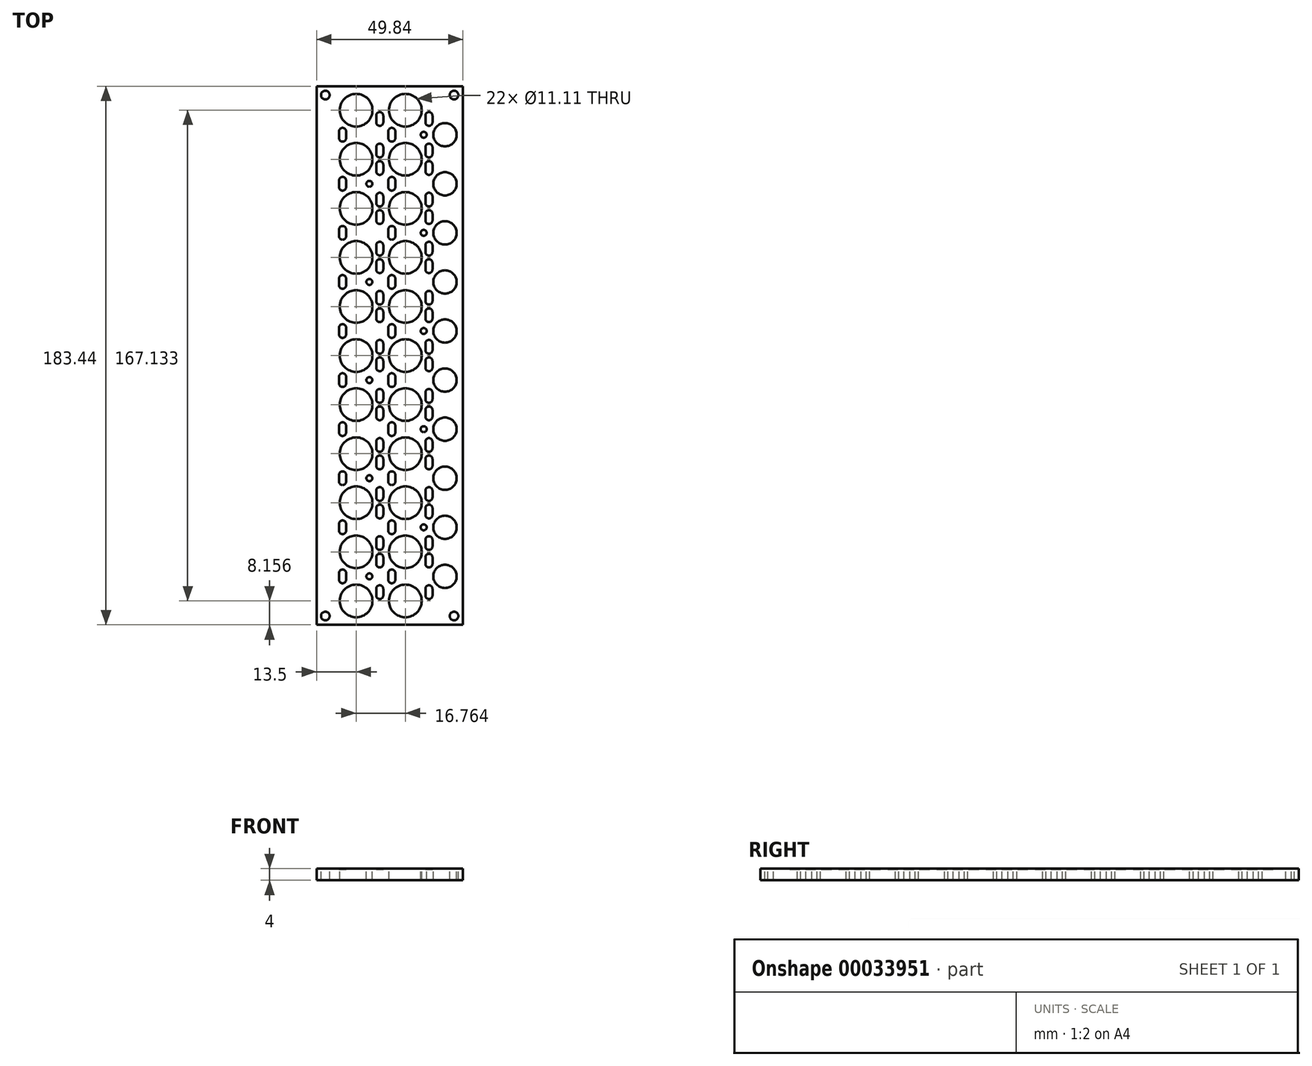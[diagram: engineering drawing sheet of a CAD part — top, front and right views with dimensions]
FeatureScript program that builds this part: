
annotation { "Feature Type Name" : "Feature", "Feature Type Description" : "" }
export const myFeature = defineFeature(function(context is Context, id is Id, definition is map)
    precondition{}
    {
        {
            var Q0;
            Q0=qCreatedBy(makeId("Top.planeOp"),FACE);
            var sketch = newSketch(context, id + "F0", { "sketchPlane" : qUnion([Q0])});
            skLineSegment(sketch, "E0.bottom", {"start": v(-3, -3) * mm, "end": v(46.84, -3) * mm});
            skLineSegment(sketch, "E0.top", {"start": v(-3, 180.44) * mm, "end": v(46.84, 180.44) * mm});
            skLineSegment(sketch, "E0.left", {"start": v(-3, -3) * mm, "end": v(-3, 180.44) * mm});
            skLineSegment(sketch, "E0.right", {"start": v(46.84, -3) * mm, "end": v(46.84, 180.44) * mm});
            skSolve(sketch);
        }
        {
            var Q0;
            Q0 = qSketchRegion(id + "F0", true);
            extrude(context, id + "F1", {"entities" : qUnion([Q0]), "oppositeDirection" : true, "depth" : 4 * mm});
        }
        {
            var Q0;
            Q0=makeQuery(id+"F1.opExtrude","CAP_FACE",FACE,{"disambiguationData":[OSD([sQuery(id+"F0.wireOp",EDGE,"E0.bottom"),sQuery(id+"F0.wireOp",EDGE,"E0.top"),sQuery(id+"F0.wireOp",EDGE,"E0.left"),sQuery(id+"F0.wireOp",EDGE,"E0.right")])],"isStart":true});
            var sketch = newSketch(context, id + "F2", { "sketchPlane" : qUnion([Q0])});
            skPoint(sketch, "E1.rect.middle", {"position": v(35.3, 141.84) * mm});
            skPoint(sketch, "E2.rect.middle", {"position": v(5.88, 30.23) * mm});
            skPoint(sketch, "E3.rect.middle", {"position": v(35.3, 8.14) * mm});
            skPoint(sketch, "E4.rect.middle", {"position": v(5.88, 97.08) * mm});
            skPoint(sketch, "E5.rect.middle", {"position": v(35.3, 102.46) * mm});
            skPoint(sketch, "E6.rect.middle", {"position": v(35.3, 158.56) * mm});
            skPoint(sketch, "E7.rect.middle", {"position": v(5.88, 63.65) * mm});
            skPoint(sketch, "E8.rect.middle", {"position": v(35.3, 35.6) * mm});
            skPoint(sketch, "E9.rect.middle", {"position": v(35.3, 24.85) * mm});
            skPoint(sketch, "E10.rect.middle", {"position": v(35.3, 125.13) * mm});
            skPoint(sketch, "E11.rect.middle", {"position": v(5.88, 130.5) * mm});
            skPoint(sketch, "E12.rect.middle", {"position": v(18.54, 169.3) * mm});
            skPoint(sketch, "E13.rect.middle", {"position": v(35.3, 41.56) * mm});
            skPoint(sketch, "E14.rect.middle", {"position": v(35.3, 74.99) * mm});
            skPoint(sketch, "E15.rect.middle", {"position": v(35.3, 108.42) * mm});
            skPoint(sketch, "E16.rect.middle", {"position": v(35.3, 169.3) * mm});
            skPoint(sketch, "E17.rect.middle", {"position": v(35.3, 91.7) * mm});
            skPoint(sketch, "E18.rect.middle", {"position": v(35.3, 69.03) * mm});
            skPoint(sketch, "E19.rect.middle", {"position": v(35.3, 58.28) * mm});
            skPoint(sketch, "E20.rect.middle", {"position": v(35.3, 135.88) * mm});
            skPoint(sketch, "E21.rect.middle", {"position": v(5.88, 163.93) * mm});
            skPoint(sketch, "E22.rect.middle", {"position": v(35.3, 52.32) * mm});
            skPoint(sketch, "E23.rect.middle", {"position": v(18.54, 141.84) * mm});
            skPoint(sketch, "E24.rect.middle", {"position": v(18.54, 69.03) * mm});
            skPoint(sketch, "E25.rect.middle", {"position": v(18.54, 35.6) * mm});
            skPoint(sketch, "E26.rect.middle", {"position": v(5.88, 113.8) * mm});
            skPoint(sketch, "E27.rect.middle", {"position": v(35.3, 152.6) * mm});
            skPoint(sketch, "E28.rect.middle", {"position": v(35.3, 85.74) * mm});
            skPoint(sketch, "E29.rect.middle", {"position": v(35.3, 119.17) * mm});
            skPoint(sketch, "E30.rect.middle", {"position": v(18.54, 58.28) * mm});
            skPoint(sketch, "E31.rect.middle", {"position": v(5.88, 147.22) * mm});
            skPoint(sketch, "E32.rect.middle", {"position": v(18.54, 135.88) * mm});
            skPoint(sketch, "E33.rect.middle", {"position": v(35.3, 18.89) * mm});
            skPoint(sketch, "E34.rect.middle", {"position": v(22.64, 13.51) * mm});
            skPoint(sketch, "E35.rect.middle", {"position": v(18.54, 102.46) * mm});
            skPoint(sketch, "E36.rect.middle", {"position": v(5.88, 46.94) * mm});
            skPoint(sketch, "E37.rect.middle", {"position": v(18.54, 74.99) * mm});
            skPoint(sketch, "E38.rect.middle", {"position": v(22.64, 80.37) * mm});
            skPoint(sketch, "E39.rect.middle", {"position": v(22.64, 147.22) * mm});
            skPoint(sketch, "E40.rect.middle", {"position": v(18.54, 108.42) * mm});
            skPoint(sketch, "E41.rect.middle", {"position": v(18.54, 8.14) * mm});
            skPoint(sketch, "E42.rect.middle", {"position": v(5.88, 13.51) * mm});
            skPoint(sketch, "E43.rect.middle", {"position": v(5.88, 80.37) * mm});
            skPoint(sketch, "E44.rect.middle", {"position": v(18.54, 41.56) * mm});
            skPoint(sketch, "E45.rect.middle", {"position": v(18.54, 125.13) * mm});
            skPoint(sketch, "E46.rect.middle", {"position": v(18.54, 24.85) * mm});
            skPoint(sketch, "E47.rect.middle", {"position": v(18.54, 85.74) * mm});
            skPoint(sketch, "E48.rect.middle", {"position": v(22.64, 30.23) * mm});
            skPoint(sketch, "E49.rect.middle", {"position": v(22.64, 113.8) * mm});
            skPoint(sketch, "E50.rect.middle", {"position": v(18.54, 91.7) * mm});
            skPoint(sketch, "E51.rect.middle", {"position": v(22.64, 97.08) * mm});
            skPoint(sketch, "E52.rect.middle", {"position": v(22.64, 163.93) * mm});
            skPoint(sketch, "E53.rect.middle", {"position": v(22.64, 130.5) * mm});
            skPoint(sketch, "E54.rect.middle", {"position": v(18.54, 152.6) * mm});
            skPoint(sketch, "E55.rect.middle", {"position": v(18.54, 119.17) * mm});
            skPoint(sketch, "E56.rect.middle", {"position": v(22.64, 63.65) * mm});
            skPoint(sketch, "E57.rect.middle", {"position": v(18.54, 18.89) * mm});
            skPoint(sketch, "E58.rect.middle", {"position": v(22.64, 46.94) * mm});
            skPoint(sketch, "E59.rect.middle", {"position": v(18.54, 158.56) * mm});
            skArc(sketch, "E60", {"start": v(4.68, 62.5) * mm, "mid": v(5.88, 61.31) * mm, "end": v(7.07, 62.5) * mm});
            skArc(sketch, "E61", {"start": v(19.73, 170.46) * mm, "mid": v(18.54, 171.65) * mm, "end": v(17.35, 170.46) * mm});
            skArc(sketch, "E62", {"start": v(34.12, 101.3) * mm, "mid": v(35.3, 100.11) * mm, "end": v(36.5, 101.3) * mm});
            skLineSegment(sketch, "E16.rect.left", {"start": v(36.5, 168.16) * mm, "end": v(36.5, 170.46) * mm});
            skArc(sketch, "E63", {"start": v(7.07, 31.38) * mm, "mid": v(5.88, 32.57) * mm, "end": v(4.68, 31.38) * mm});
            skLineSegment(sketch, "E8.rect.right", {"start": v(34.12, 34.45) * mm, "end": v(34.12, 36.75) * mm});
            skArc(sketch, "E64", {"start": v(34.12, 34.45) * mm, "mid": v(35.3, 33.26) * mm, "end": v(36.5, 34.45) * mm});
            skLineSegment(sketch, "E16.rect.right", {"start": v(34.12, 168.16) * mm, "end": v(34.12, 170.46) * mm});
            skPoint(sketch, "E65.rect.middle", {"position": v(18.54, 52.32) * mm});
            skArc(sketch, "E66", {"start": v(34.12, 168.16) * mm, "mid": v(35.3, 166.97) * mm, "end": v(36.5, 168.16) * mm});
            skLineSegment(sketch, "E8.rect.left", {"start": v(36.5, 34.45) * mm, "end": v(36.5, 36.75) * mm});
            skArc(sketch, "E67", {"start": v(4.68, 129.36) * mm, "mid": v(5.88, 128.16) * mm, "end": v(7.07, 129.36) * mm});
            skArc(sketch, "E68", {"start": v(36.5, 126.28) * mm, "mid": v(35.3, 127.47) * mm, "end": v(34.12, 126.28) * mm});
            skArc(sketch, "E69", {"start": v(36.5, 170.46) * mm, "mid": v(35.3, 171.65) * mm, "end": v(34.12, 170.46) * mm});
            skArc(sketch, "E70", {"start": v(7.07, 81.52) * mm, "mid": v(5.88, 82.7) * mm, "end": v(4.68, 81.52) * mm});
            skArc(sketch, "E71", {"start": v(7.07, 131.66) * mm, "mid": v(5.88, 132.85) * mm, "end": v(4.68, 131.66) * mm});
            skLineSegment(sketch, "E29.rect.right", {"start": v(34.12, 118.02) * mm, "end": v(34.12, 120.32) * mm});
            skLineSegment(sketch, "E12.rect.right", {"start": v(17.35, 168.16) * mm, "end": v(17.35, 170.46) * mm});
            skArc(sketch, "E72", {"start": v(17.35, 168.16) * mm, "mid": v(18.54, 166.97) * mm, "end": v(19.73, 168.16) * mm});
            skArc(sketch, "E73", {"start": v(36.5, 59.43) * mm, "mid": v(35.3, 60.62) * mm, "end": v(34.12, 59.43) * mm});
            skArc(sketch, "E74", {"start": v(19.73, 126.28) * mm, "mid": v(18.54, 127.47) * mm, "end": v(17.35, 126.28) * mm});
            skArc(sketch, "E75", {"start": v(36.5, 76.14) * mm, "mid": v(35.3, 77.33) * mm, "end": v(34.12, 76.14) * mm});
            skArc(sketch, "E76", {"start": v(36.5, 159.7) * mm, "mid": v(35.3, 160.9) * mm, "end": v(34.12, 159.7) * mm});
            skLineSegment(sketch, "E5.rect.left", {"start": v(36.5, 101.3) * mm, "end": v(36.5, 103.6) * mm});
            skArc(sketch, "E77", {"start": v(7.07, 48.09) * mm, "mid": v(5.88, 49.28) * mm, "end": v(4.68, 48.09) * mm});
            skArc(sketch, "E78", {"start": v(7.07, 114.94) * mm, "mid": v(5.88, 116.13) * mm, "end": v(4.68, 114.94) * mm});
            skLineSegment(sketch, "E22.rect.right", {"start": v(34.12, 51.17) * mm, "end": v(34.12, 53.47) * mm});
            skArc(sketch, "E79", {"start": v(34.12, 151.45) * mm, "mid": v(35.3, 150.25) * mm, "end": v(36.5, 151.45) * mm});
            skLineSegment(sketch, "E13.rect.left", {"start": v(36.5, 40.41) * mm, "end": v(36.5, 42.71) * mm});
            skLineSegment(sketch, "E4.rect.left", {"start": v(7.07, 95.93) * mm, "end": v(7.07, 98.23) * mm});
            skArc(sketch, "E80", {"start": v(36.5, 9.29) * mm, "mid": v(35.3, 10.48) * mm, "end": v(34.12, 9.29) * mm});
            skLineSegment(sketch, "E4.rect.right", {"start": v(4.68, 95.93) * mm, "end": v(4.68, 98.23) * mm});
            skArc(sketch, "E81", {"start": v(36.5, 53.47) * mm, "mid": v(35.3, 54.66) * mm, "end": v(34.12, 53.47) * mm});
            skArc(sketch, "E82", {"start": v(34.12, 6.99) * mm, "mid": v(35.3, 5.8) * mm, "end": v(36.5, 6.99) * mm});
            skLineSegment(sketch, "E13.rect.right", {"start": v(34.12, 40.41) * mm, "end": v(34.12, 42.71) * mm});
            skLineSegment(sketch, "E3.rect.left", {"start": v(36.5, 6.99) * mm, "end": v(36.5, 9.29) * mm});
            skArc(sketch, "E83", {"start": v(34.12, 40.41) * mm, "mid": v(35.3, 39.22) * mm, "end": v(36.5, 40.41) * mm});
            skArc(sketch, "E84", {"start": v(34.12, 107.27) * mm, "mid": v(35.3, 106.07) * mm, "end": v(36.5, 107.27) * mm});
            skArc(sketch, "E85", {"start": v(34.12, 51.17) * mm, "mid": v(35.3, 49.98) * mm, "end": v(36.5, 51.17) * mm});
            skLineSegment(sketch, "E15.rect.left", {"start": v(36.5, 107.27) * mm, "end": v(36.5, 109.57) * mm});
            skLineSegment(sketch, "E3.rect.right", {"start": v(34.12, 6.99) * mm, "end": v(34.12, 9.29) * mm});
            skArc(sketch, "E86", {"start": v(34.12, 17.74) * mm, "mid": v(35.3, 16.55) * mm, "end": v(36.5, 17.74) * mm});
            skArc(sketch, "E87", {"start": v(4.68, 29.08) * mm, "mid": v(5.88, 27.88) * mm, "end": v(7.07, 29.08) * mm});
            skArc(sketch, "E88", {"start": v(4.68, 162.78) * mm, "mid": v(5.88, 161.6) * mm, "end": v(7.07, 162.78) * mm});
            skLineSegment(sketch, "E11.rect.left", {"start": v(7.07, 129.36) * mm, "end": v(7.07, 131.66) * mm});
            skLineSegment(sketch, "E21.rect.right", {"start": v(4.68, 162.78) * mm, "end": v(4.68, 165.08) * mm});
            skLineSegment(sketch, "E7.rect.right", {"start": v(4.68, 62.5) * mm, "end": v(4.68, 64.8) * mm});
            skArc(sketch, "E89", {"start": v(34.12, 67.88) * mm, "mid": v(35.3, 66.69) * mm, "end": v(36.5, 67.88) * mm});
            skLineSegment(sketch, "E5.rect.right", {"start": v(34.12, 101.3) * mm, "end": v(34.12, 103.6) * mm});
            skLineSegment(sketch, "E7.rect.left", {"start": v(7.07, 62.5) * mm, "end": v(7.07, 64.8) * mm});
            skLineSegment(sketch, "E18.rect.right", {"start": v(34.12, 67.88) * mm, "end": v(34.12, 70.18) * mm});
            skArc(sketch, "E90", {"start": v(36.5, 103.6) * mm, "mid": v(35.3, 104.8) * mm, "end": v(34.12, 103.6) * mm});
            skLineSegment(sketch, "E12.rect.left", {"start": v(19.73, 168.16) * mm, "end": v(19.73, 170.46) * mm});
            skLineSegment(sketch, "E18.rect.left", {"start": v(36.5, 67.88) * mm, "end": v(36.5, 70.18) * mm});
            skLineSegment(sketch, "E15.rect.right", {"start": v(34.12, 107.27) * mm, "end": v(34.12, 109.57) * mm});
            skArc(sketch, "E91", {"start": v(36.5, 36.75) * mm, "mid": v(35.3, 37.94) * mm, "end": v(34.12, 36.75) * mm});
            skArc(sketch, "E92", {"start": v(4.68, 95.93) * mm, "mid": v(5.88, 94.74) * mm, "end": v(7.07, 95.93) * mm});
            skLineSegment(sketch, "E26.rect.right", {"start": v(4.68, 112.64) * mm, "end": v(4.68, 114.94) * mm});
            skArc(sketch, "E93", {"start": v(36.5, 109.57) * mm, "mid": v(35.3, 110.76) * mm, "end": v(34.12, 109.57) * mm});
            skLineSegment(sketch, "E26.rect.left", {"start": v(7.07, 112.64) * mm, "end": v(7.07, 114.94) * mm});
            skArc(sketch, "E94", {"start": v(7.07, 98.23) * mm, "mid": v(5.88, 99.42) * mm, "end": v(4.68, 98.23) * mm});
            skLineSegment(sketch, "E36.rect.right", {"start": v(4.68, 45.79) * mm, "end": v(4.68, 48.09) * mm});
            skArc(sketch, "E95", {"start": v(36.5, 143) * mm, "mid": v(35.3, 144.18) * mm, "end": v(34.12, 143) * mm});
            skArc(sketch, "E96", {"start": v(4.68, 45.79) * mm, "mid": v(5.88, 44.6) * mm, "end": v(7.07, 45.79) * mm});
            skArc(sketch, "E97", {"start": v(19.73, 9.29) * mm, "mid": v(18.54, 10.48) * mm, "end": v(17.35, 9.29) * mm});
            skArc(sketch, "E98", {"start": v(4.68, 112.64) * mm, "mid": v(5.88, 111.45) * mm, "end": v(7.07, 112.64) * mm});
            skLineSegment(sketch, "E22.rect.left", {"start": v(36.5, 51.17) * mm, "end": v(36.5, 53.47) * mm});
            skLineSegment(sketch, "E11.rect.right", {"start": v(4.68, 129.36) * mm, "end": v(4.68, 131.66) * mm});
            skArc(sketch, "E99", {"start": v(7.07, 165.08) * mm, "mid": v(5.88, 166.27) * mm, "end": v(4.68, 165.08) * mm});
            skArc(sketch, "E100", {"start": v(7.07, 64.8) * mm, "mid": v(5.88, 66) * mm, "end": v(4.68, 64.8) * mm});
            skArc(sketch, "E101", {"start": v(17.35, 6.99) * mm, "mid": v(18.54, 5.8) * mm, "end": v(19.73, 6.99) * mm});
            skArc(sketch, "E102", {"start": v(36.5, 42.71) * mm, "mid": v(35.3, 43.9) * mm, "end": v(34.12, 42.71) * mm});
            skArc(sketch, "E103", {"start": v(36.5, 92.85) * mm, "mid": v(35.3, 94.04) * mm, "end": v(34.12, 92.85) * mm});
            skLineSegment(sketch, "E36.rect.left", {"start": v(7.07, 45.79) * mm, "end": v(7.07, 48.09) * mm});
            skLineSegment(sketch, "E29.rect.left", {"start": v(36.5, 118.02) * mm, "end": v(36.5, 120.32) * mm});
            skArc(sketch, "E104", {"start": v(34.12, 118.02) * mm, "mid": v(35.3, 116.83) * mm, "end": v(36.5, 118.02) * mm});
            skLineSegment(sketch, "E21.rect.left", {"start": v(7.07, 162.78) * mm, "end": v(7.07, 165.08) * mm});
            skArc(sketch, "E105", {"start": v(4.68, 146.07) * mm, "mid": v(5.88, 144.88) * mm, "end": v(7.07, 146.07) * mm});
            skLineSegment(sketch, "E2.rect.left", {"start": v(7.07, 29.08) * mm, "end": v(7.07, 31.38) * mm});
            skLineSegment(sketch, "E2.rect.right", {"start": v(4.68, 29.08) * mm, "end": v(4.68, 31.38) * mm});
            skLineSegment(sketch, "E41.rect.left", {"start": v(19.73, 6.99) * mm, "end": v(19.73, 9.29) * mm});
            skLineSegment(sketch, "E41.rect.right", {"start": v(17.35, 6.99) * mm, "end": v(17.35, 9.29) * mm});
            skArc(sketch, "E106", {"start": v(23.83, 48.09) * mm, "mid": v(22.64, 49.28) * mm, "end": v(21.45, 48.09) * mm});
            skArc(sketch, "E107", {"start": v(21.45, 29.08) * mm, "mid": v(22.64, 27.88) * mm, "end": v(23.83, 29.08) * mm});
            skLineSegment(sketch, "E48.rect.right", {"start": v(21.45, 29.08) * mm, "end": v(21.45, 31.38) * mm});
            skArc(sketch, "E108", {"start": v(19.73, 109.57) * mm, "mid": v(18.54, 110.76) * mm, "end": v(17.35, 109.57) * mm});
            skLineSegment(sketch, "E47.rect.left", {"start": v(19.73, 84.6) * mm, "end": v(19.73, 86.9) * mm});
            skLineSegment(sketch, "E24.rect.left", {"start": v(19.73, 67.88) * mm, "end": v(19.73, 70.18) * mm});
            skArc(sketch, "E109", {"start": v(23.83, 14.66) * mm, "mid": v(22.64, 15.85) * mm, "end": v(21.45, 14.66) * mm});
            skLineSegment(sketch, "E20.rect.right", {"start": v(34.12, 134.73) * mm, "end": v(34.12, 137.03) * mm});
            skLineSegment(sketch, "E31.rect.right", {"start": v(4.68, 146.07) * mm, "end": v(4.68, 148.37) * mm});
            skLineSegment(sketch, "E6.rect.left", {"start": v(36.5, 157.4) * mm, "end": v(36.5, 159.7) * mm});
            skArc(sketch, "E110", {"start": v(21.45, 12.36) * mm, "mid": v(22.64, 11.17) * mm, "end": v(23.83, 12.36) * mm});
            skArc(sketch, "E111", {"start": v(4.68, 79.22) * mm, "mid": v(5.88, 78.02) * mm, "end": v(7.07, 79.22) * mm});
            skLineSegment(sketch, "E28.rect.right", {"start": v(34.12, 84.6) * mm, "end": v(34.12, 86.9) * mm});
            skLineSegment(sketch, "E39.rect.left", {"start": v(23.83, 146.07) * mm, "end": v(23.83, 148.37) * mm});
            skArc(sketch, "E112", {"start": v(21.45, 79.22) * mm, "mid": v(22.64, 78.02) * mm, "end": v(23.83, 79.22) * mm});
            skArc(sketch, "E113", {"start": v(17.35, 73.84) * mm, "mid": v(18.54, 72.65) * mm, "end": v(19.73, 73.84) * mm});
            skArc(sketch, "E114", {"start": v(21.45, 146.07) * mm, "mid": v(22.64, 144.88) * mm, "end": v(23.83, 146.07) * mm});
            skLineSegment(sketch, "E10.rect.right", {"start": v(34.12, 123.98) * mm, "end": v(34.12, 126.28) * mm});
            skLineSegment(sketch, "E37.rect.right", {"start": v(17.35, 73.84) * mm, "end": v(17.35, 76.14) * mm});
            skLineSegment(sketch, "E31.rect.left", {"start": v(7.07, 146.07) * mm, "end": v(7.07, 148.37) * mm});
            skArc(sketch, "E115", {"start": v(17.35, 40.41) * mm, "mid": v(18.54, 39.22) * mm, "end": v(19.73, 40.41) * mm});
            skArc(sketch, "E116", {"start": v(4.68, 12.36) * mm, "mid": v(5.88, 11.17) * mm, "end": v(7.07, 12.36) * mm});
            skLineSegment(sketch, "E17.rect.left", {"start": v(36.5, 90.55) * mm, "end": v(36.5, 92.85) * mm});
            skLineSegment(sketch, "E10.rect.left", {"start": v(36.5, 123.98) * mm, "end": v(36.5, 126.28) * mm});
            skArc(sketch, "E117", {"start": v(34.12, 140.7) * mm, "mid": v(35.3, 139.5) * mm, "end": v(36.5, 140.7) * mm});
            skArc(sketch, "E118", {"start": v(7.07, 14.66) * mm, "mid": v(5.88, 15.85) * mm, "end": v(4.68, 14.66) * mm});
            skArc(sketch, "E119", {"start": v(19.73, 70.18) * mm, "mid": v(18.54, 71.37) * mm, "end": v(17.35, 70.18) * mm});
            skArc(sketch, "E120", {"start": v(36.5, 20.04) * mm, "mid": v(35.3, 21.23) * mm, "end": v(34.12, 20.04) * mm});
            skLineSegment(sketch, "E35.rect.right", {"start": v(17.35, 101.3) * mm, "end": v(17.35, 103.6) * mm});
            skArc(sketch, "E121", {"start": v(34.12, 84.6) * mm, "mid": v(35.3, 83.4) * mm, "end": v(36.5, 84.6) * mm});
            skLineSegment(sketch, "E40.rect.left", {"start": v(19.73, 107.27) * mm, "end": v(19.73, 109.57) * mm});
            skLineSegment(sketch, "E24.rect.right", {"start": v(17.35, 67.88) * mm, "end": v(17.35, 70.18) * mm});
            skLineSegment(sketch, "E20.rect.left", {"start": v(36.5, 134.73) * mm, "end": v(36.5, 137.03) * mm});
            skLineSegment(sketch, "E38.rect.right", {"start": v(21.45, 79.22) * mm, "end": v(21.45, 81.52) * mm});
            skLineSegment(sketch, "E32.rect.right", {"start": v(17.35, 134.73) * mm, "end": v(17.35, 137.03) * mm});
            skLineSegment(sketch, "E27.rect.right", {"start": v(34.12, 151.45) * mm, "end": v(34.12, 153.75) * mm});
            skLineSegment(sketch, "E33.rect.left", {"start": v(36.5, 17.74) * mm, "end": v(36.5, 20.04) * mm});
            skArc(sketch, "E122", {"start": v(34.12, 23.7) * mm, "mid": v(35.3, 22.5) * mm, "end": v(36.5, 23.7) * mm});
            skArc(sketch, "E123", {"start": v(19.73, 36.75) * mm, "mid": v(18.54, 37.94) * mm, "end": v(17.35, 36.75) * mm});
            skLineSegment(sketch, "E14.rect.right", {"start": v(34.12, 73.84) * mm, "end": v(34.12, 76.14) * mm});
            skArc(sketch, "E124", {"start": v(17.35, 107.27) * mm, "mid": v(18.54, 106.07) * mm, "end": v(19.73, 107.27) * mm});
            skArc(sketch, "E125", {"start": v(34.12, 157.4) * mm, "mid": v(35.3, 156.21) * mm, "end": v(36.5, 157.4) * mm});
            skLineSegment(sketch, "E40.rect.right", {"start": v(17.35, 107.27) * mm, "end": v(17.35, 109.57) * mm});
            skLineSegment(sketch, "E23.rect.left", {"start": v(19.73, 140.7) * mm, "end": v(19.73, 143) * mm});
            skLineSegment(sketch, "E33.rect.right", {"start": v(34.12, 17.74) * mm, "end": v(34.12, 20.04) * mm});
            skLineSegment(sketch, "E44.rect.left", {"start": v(19.73, 40.41) * mm, "end": v(19.73, 42.71) * mm});
            skArc(sketch, "E126", {"start": v(36.5, 26) * mm, "mid": v(35.3, 27.19) * mm, "end": v(34.12, 26) * mm});
            skArc(sketch, "E127", {"start": v(17.35, 34.45) * mm, "mid": v(18.54, 33.26) * mm, "end": v(19.73, 34.45) * mm});
            skArc(sketch, "E128", {"start": v(36.5, 86.9) * mm, "mid": v(35.3, 88.08) * mm, "end": v(34.12, 86.9) * mm});
            skArc(sketch, "E129", {"start": v(17.35, 84.6) * mm, "mid": v(18.54, 83.4) * mm, "end": v(19.73, 84.6) * mm});
            skArc(sketch, "E130", {"start": v(19.73, 143) * mm, "mid": v(18.54, 144.18) * mm, "end": v(17.35, 143) * mm});
            skLineSegment(sketch, "E28.rect.left", {"start": v(36.5, 84.6) * mm, "end": v(36.5, 86.9) * mm});
            skLineSegment(sketch, "E1.rect.left", {"start": v(36.5, 140.7) * mm, "end": v(36.5, 143) * mm});
            skArc(sketch, "E131", {"start": v(36.5, 137.03) * mm, "mid": v(35.3, 138.22) * mm, "end": v(34.12, 137.03) * mm});
            skArc(sketch, "E132", {"start": v(34.12, 73.84) * mm, "mid": v(35.3, 72.65) * mm, "end": v(36.5, 73.84) * mm});
            skArc(sketch, "E133", {"start": v(7.07, 148.37) * mm, "mid": v(5.88, 149.56) * mm, "end": v(4.68, 148.37) * mm});
            skLineSegment(sketch, "E43.rect.right", {"start": v(4.68, 79.22) * mm, "end": v(4.68, 81.52) * mm});
            skLineSegment(sketch, "E47.rect.right", {"start": v(17.35, 84.6) * mm, "end": v(17.35, 86.9) * mm});
            skLineSegment(sketch, "E39.rect.right", {"start": v(21.45, 146.07) * mm, "end": v(21.45, 148.37) * mm});
            skLineSegment(sketch, "E34.rect.right", {"start": v(21.45, 12.36) * mm, "end": v(21.45, 14.66) * mm});
            skArc(sketch, "E134", {"start": v(36.5, 70.18) * mm, "mid": v(35.3, 71.37) * mm, "end": v(34.12, 70.18) * mm});
            skLineSegment(sketch, "E17.rect.right", {"start": v(34.12, 90.55) * mm, "end": v(34.12, 92.85) * mm});
            skArc(sketch, "E135", {"start": v(34.12, 123.98) * mm, "mid": v(35.3, 122.79) * mm, "end": v(36.5, 123.98) * mm});
            skLineSegment(sketch, "E14.rect.left", {"start": v(36.5, 73.84) * mm, "end": v(36.5, 76.14) * mm});
            skLineSegment(sketch, "E23.rect.right", {"start": v(17.35, 140.7) * mm, "end": v(17.35, 143) * mm});
            skLineSegment(sketch, "E43.rect.left", {"start": v(7.07, 79.22) * mm, "end": v(7.07, 81.52) * mm});
            skLineSegment(sketch, "E34.rect.left", {"start": v(23.83, 12.36) * mm, "end": v(23.83, 14.66) * mm});
            skLineSegment(sketch, "E44.rect.right", {"start": v(17.35, 40.41) * mm, "end": v(17.35, 42.71) * mm});
            skArc(sketch, "E136", {"start": v(36.5, 120.32) * mm, "mid": v(35.3, 121.5) * mm, "end": v(34.12, 120.32) * mm});
            skLineSegment(sketch, "E1.rect.right", {"start": v(34.12, 140.7) * mm, "end": v(34.12, 143) * mm});
            skArc(sketch, "E137", {"start": v(36.5, 153.75) * mm, "mid": v(35.3, 154.94) * mm, "end": v(34.12, 153.75) * mm});
            skArc(sketch, "E138", {"start": v(23.83, 64.8) * mm, "mid": v(22.64, 66) * mm, "end": v(21.45, 64.8) * mm});
            skArc(sketch, "E139", {"start": v(17.35, 17.74) * mm, "mid": v(18.54, 16.55) * mm, "end": v(19.73, 17.74) * mm});
            skArc(sketch, "E140", {"start": v(19.73, 42.71) * mm, "mid": v(18.54, 43.9) * mm, "end": v(17.35, 42.71) * mm});
            skArc(sketch, "E141", {"start": v(34.12, 134.73) * mm, "mid": v(35.3, 133.54) * mm, "end": v(36.5, 134.73) * mm});
            skArc(sketch, "E142", {"start": v(17.35, 101.3) * mm, "mid": v(18.54, 100.11) * mm, "end": v(19.73, 101.3) * mm});
            skLineSegment(sketch, "E35.rect.left", {"start": v(19.73, 101.3) * mm, "end": v(19.73, 103.6) * mm});
            skArc(sketch, "E143", {"start": v(17.35, 140.7) * mm, "mid": v(18.54, 139.5) * mm, "end": v(19.73, 140.7) * mm});
            skLineSegment(sketch, "E9.rect.left", {"start": v(36.5, 23.7) * mm, "end": v(36.5, 26) * mm});
            skArc(sketch, "E144", {"start": v(19.73, 76.14) * mm, "mid": v(18.54, 77.33) * mm, "end": v(17.35, 76.14) * mm});
            skArc(sketch, "E145", {"start": v(17.35, 67.88) * mm, "mid": v(18.54, 66.69) * mm, "end": v(19.73, 67.88) * mm});
            skArc(sketch, "E146", {"start": v(19.73, 137.03) * mm, "mid": v(18.54, 138.22) * mm, "end": v(17.35, 137.03) * mm});
            skLineSegment(sketch, "E38.rect.left", {"start": v(23.83, 79.22) * mm, "end": v(23.83, 81.52) * mm});
            skLineSegment(sketch, "E27.rect.left", {"start": v(36.5, 151.45) * mm, "end": v(36.5, 153.75) * mm});
            skArc(sketch, "E147", {"start": v(17.35, 151.45) * mm, "mid": v(18.54, 150.25) * mm, "end": v(19.73, 151.45) * mm});
            skLineSegment(sketch, "E48.rect.left", {"start": v(23.83, 29.08) * mm, "end": v(23.83, 31.38) * mm});
            skArc(sketch, "E148", {"start": v(23.83, 81.52) * mm, "mid": v(22.64, 82.7) * mm, "end": v(21.45, 81.52) * mm});
            skLineSegment(sketch, "E37.rect.left", {"start": v(19.73, 73.84) * mm, "end": v(19.73, 76.14) * mm});
            skLineSegment(sketch, "E32.rect.left", {"start": v(19.73, 134.73) * mm, "end": v(19.73, 137.03) * mm});
            skArc(sketch, "E149", {"start": v(34.12, 90.55) * mm, "mid": v(35.3, 89.36) * mm, "end": v(36.5, 90.55) * mm});
            skLineSegment(sketch, "E6.rect.right", {"start": v(34.12, 157.4) * mm, "end": v(34.12, 159.7) * mm});
            skArc(sketch, "E150", {"start": v(23.83, 31.38) * mm, "mid": v(22.64, 32.57) * mm, "end": v(21.45, 31.38) * mm});
            skLineSegment(sketch, "E9.rect.right", {"start": v(34.12, 23.7) * mm, "end": v(34.12, 26) * mm});
            skArc(sketch, "E151", {"start": v(17.35, 134.73) * mm, "mid": v(18.54, 133.54) * mm, "end": v(19.73, 134.73) * mm});
            skArc(sketch, "E152", {"start": v(19.73, 103.6) * mm, "mid": v(18.54, 104.8) * mm, "end": v(17.35, 103.6) * mm});
            skArc(sketch, "E153", {"start": v(23.83, 148.37) * mm, "mid": v(22.64, 149.56) * mm, "end": v(21.45, 148.37) * mm});
            skLineSegment(sketch, "E25.rect.right", {"start": v(17.35, 34.45) * mm, "end": v(17.35, 36.75) * mm});
            skLineSegment(sketch, "E42.rect.right", {"start": v(4.68, 12.36) * mm, "end": v(4.68, 14.66) * mm});
            skLineSegment(sketch, "E42.rect.left", {"start": v(7.07, 12.36) * mm, "end": v(7.07, 14.66) * mm});
            skLineSegment(sketch, "E25.rect.left", {"start": v(19.73, 34.45) * mm, "end": v(19.73, 36.75) * mm});
            skLineSegment(sketch, "E53.rect.left", {"start": v(23.83, 129.36) * mm, "end": v(23.83, 131.66) * mm});
            skLineSegment(sketch, "E19.rect.right", {"start": v(34.12, 57.13) * mm, "end": v(34.12, 59.43) * mm});
            skLineSegment(sketch, "E49.rect.right", {"start": v(21.45, 112.64) * mm, "end": v(21.45, 114.94) * mm});
            skLineSegment(sketch, "E50.rect.left", {"start": v(19.73, 90.55) * mm, "end": v(19.73, 92.85) * mm});
            skArc(sketch, "E154", {"start": v(19.73, 53.47) * mm, "mid": v(18.54, 54.66) * mm, "end": v(17.35, 53.47) * mm});
            skArc(sketch, "E155", {"start": v(17.35, 90.55) * mm, "mid": v(18.54, 89.36) * mm, "end": v(19.73, 90.55) * mm});
            skLineSegment(sketch, "E50.rect.right", {"start": v(17.35, 90.55) * mm, "end": v(17.35, 92.85) * mm});
            skLineSegment(sketch, "E52.rect.left", {"start": v(23.83, 162.78) * mm, "end": v(23.83, 165.08) * mm});
            skLineSegment(sketch, "E55.rect.left", {"start": v(19.73, 118.02) * mm, "end": v(19.73, 120.32) * mm});
            skLineSegment(sketch, "E46.rect.right", {"start": v(17.35, 23.7) * mm, "end": v(17.35, 26) * mm});
            skArc(sketch, "E156", {"start": v(17.35, 157.4) * mm, "mid": v(18.54, 156.21) * mm, "end": v(19.73, 157.4) * mm});
            skLineSegment(sketch, "E59.rect.right", {"start": v(17.35, 157.4) * mm, "end": v(17.35, 159.7) * mm});
            skLineSegment(sketch, "E46.rect.left", {"start": v(19.73, 23.7) * mm, "end": v(19.73, 26) * mm});
            skLineSegment(sketch, "E30.rect.left", {"start": v(19.73, 57.13) * mm, "end": v(19.73, 59.43) * mm});
            skArc(sketch, "E157", {"start": v(19.73, 120.32) * mm, "mid": v(18.54, 121.5) * mm, "end": v(17.35, 120.32) * mm});
            skArc(sketch, "E158", {"start": v(21.45, 112.64) * mm, "mid": v(22.64, 111.45) * mm, "end": v(23.83, 112.64) * mm});
            skArc(sketch, "E159", {"start": v(21.45, 95.93) * mm, "mid": v(22.64, 94.74) * mm, "end": v(23.83, 95.93) * mm});
            skLineSegment(sketch, "E52.rect.right", {"start": v(21.45, 162.78) * mm, "end": v(21.45, 165.08) * mm});
            skLineSegment(sketch, "E54.rect.left", {"start": v(19.73, 151.45) * mm, "end": v(19.73, 153.75) * mm});
            skArc(sketch, "E160", {"start": v(19.73, 153.75) * mm, "mid": v(18.54, 154.94) * mm, "end": v(17.35, 153.75) * mm});
            skLineSegment(sketch, "E45.rect.right", {"start": v(17.35, 123.98) * mm, "end": v(17.35, 126.28) * mm});
            skLineSegment(sketch, "E30.rect.right", {"start": v(17.35, 57.13) * mm, "end": v(17.35, 59.43) * mm});
            skArc(sketch, "E161", {"start": v(17.35, 123.98) * mm, "mid": v(18.54, 122.79) * mm, "end": v(19.73, 123.98) * mm});
            skArc(sketch, "E162", {"start": v(19.73, 92.85) * mm, "mid": v(18.54, 94.04) * mm, "end": v(17.35, 92.85) * mm});
            skArc(sketch, "E163", {"start": v(34.12, 57.13) * mm, "mid": v(35.3, 55.93) * mm, "end": v(36.5, 57.13) * mm});
            skLineSegment(sketch, "E55.rect.right", {"start": v(17.35, 118.02) * mm, "end": v(17.35, 120.32) * mm});
            skLineSegment(sketch, "E51.rect.left", {"start": v(23.83, 95.93) * mm, "end": v(23.83, 98.23) * mm});
            skLineSegment(sketch, "E54.rect.right", {"start": v(17.35, 151.45) * mm, "end": v(17.35, 153.75) * mm});
            skLineSegment(sketch, "E49.rect.left", {"start": v(23.83, 112.64) * mm, "end": v(23.83, 114.94) * mm});
            skLineSegment(sketch, "E45.rect.left", {"start": v(19.73, 123.98) * mm, "end": v(19.73, 126.28) * mm});
            skLineSegment(sketch, "E58.rect.right", {"start": v(21.45, 45.79) * mm, "end": v(21.45, 48.09) * mm});
            skArc(sketch, "E164", {"start": v(19.73, 26) * mm, "mid": v(18.54, 27.19) * mm, "end": v(17.35, 26) * mm});
            skArc(sketch, "E165", {"start": v(21.45, 45.79) * mm, "mid": v(22.64, 44.6) * mm, "end": v(23.83, 45.79) * mm});
            skLineSegment(sketch, "E53.rect.right", {"start": v(21.45, 129.36) * mm, "end": v(21.45, 131.66) * mm});
            skArc(sketch, "E166", {"start": v(17.35, 23.7) * mm, "mid": v(18.54, 22.5) * mm, "end": v(19.73, 23.7) * mm});
            skLineSegment(sketch, "E58.rect.left", {"start": v(23.83, 45.79) * mm, "end": v(23.83, 48.09) * mm});
            skLineSegment(sketch, "E59.rect.left", {"start": v(19.73, 157.4) * mm, "end": v(19.73, 159.7) * mm});
            skArc(sketch, "E167", {"start": v(21.45, 162.78) * mm, "mid": v(22.64, 161.6) * mm, "end": v(23.83, 162.78) * mm});
            skArc(sketch, "E168", {"start": v(19.73, 59.43) * mm, "mid": v(18.54, 60.62) * mm, "end": v(17.35, 59.43) * mm});
            skArc(sketch, "E169", {"start": v(19.73, 20.04) * mm, "mid": v(18.54, 21.23) * mm, "end": v(17.35, 20.04) * mm});
            skArc(sketch, "E170", {"start": v(23.83, 131.66) * mm, "mid": v(22.64, 132.85) * mm, "end": v(21.45, 131.66) * mm});
            skLineSegment(sketch, "E19.rect.left", {"start": v(36.5, 57.13) * mm, "end": v(36.5, 59.43) * mm});
            skArc(sketch, "E171", {"start": v(21.45, 129.36) * mm, "mid": v(22.64, 128.16) * mm, "end": v(23.83, 129.36) * mm});
            skArc(sketch, "E172", {"start": v(19.73, 86.9) * mm, "mid": v(18.54, 88.08) * mm, "end": v(17.35, 86.9) * mm});
            skArc(sketch, "E173", {"start": v(23.83, 98.23) * mm, "mid": v(22.64, 99.42) * mm, "end": v(21.45, 98.23) * mm});
            skArc(sketch, "E174", {"start": v(23.83, 165.08) * mm, "mid": v(22.64, 166.27) * mm, "end": v(21.45, 165.08) * mm});
            skArc(sketch, "E175", {"start": v(17.35, 118.02) * mm, "mid": v(18.54, 116.83) * mm, "end": v(19.73, 118.02) * mm});
            skArc(sketch, "E176", {"start": v(17.35, 57.13) * mm, "mid": v(18.54, 55.93) * mm, "end": v(19.73, 57.13) * mm});
            skLineSegment(sketch, "E51.rect.right", {"start": v(21.45, 95.93) * mm, "end": v(21.45, 98.23) * mm});
            skArc(sketch, "E177", {"start": v(19.73, 159.7) * mm, "mid": v(18.54, 160.9) * mm, "end": v(17.35, 159.7) * mm});
            skArc(sketch, "E178", {"start": v(23.83, 114.94) * mm, "mid": v(22.64, 116.13) * mm, "end": v(21.45, 114.94) * mm});
            skLineSegment(sketch, "E57.rect.left", {"start": v(19.73, 17.74) * mm, "end": v(19.73, 20.04) * mm});
            skLineSegment(sketch, "E57.rect.right", {"start": v(17.35, 17.74) * mm, "end": v(17.35, 20.04) * mm});
            skLineSegment(sketch, "E56.rect.left", {"start": v(23.83, 62.5) * mm, "end": v(23.83, 64.8) * mm});
            skLineSegment(sketch, "E65.rect.right", {"start": v(17.35, 51.17) * mm, "end": v(17.35, 53.47) * mm});
            skLineSegment(sketch, "E56.rect.right", {"start": v(21.45, 62.5) * mm, "end": v(21.45, 64.8) * mm});
            skLineSegment(sketch, "E65.rect.left", {"start": v(19.73, 51.17) * mm, "end": v(19.73, 53.47) * mm});
            skArc(sketch, "E179", {"start": v(21.45, 62.5) * mm, "mid": v(22.64, 61.31) * mm, "end": v(23.83, 62.5) * mm});
            skArc(sketch, "E180", {"start": v(17.35, 51.17) * mm, "mid": v(18.54, 49.98) * mm, "end": v(19.73, 51.17) * mm});
            skSolve(sketch);
        }
        {
            var Q0;
            Q0 = qSketchRegion(id + "F2", true);
            extrude(context, id + "F3", {"entities" : qUnion([Q0]), "operationType" : NewBodyOperationType.REMOVE, "oppositeDirection" : true, "depth" : .3 * mm});
        }
        {
            var Q0;
            Q0=makeQuery(id+"F1.opExtrude","CAP_FACE",FACE,{"disambiguationData":[OSD([sQuery(id+"F0.wireOp",EDGE,"E0.bottom"),sQuery(id+"F0.wireOp",EDGE,"E0.top"),sQuery(id+"F0.wireOp",EDGE,"E0.left"),sQuery(id+"F0.wireOp",EDGE,"E0.right")])],"isStart":true});
            var sketch = newSketch(context, id + "F4", { "sketchPlane" : qUnion([Q0])});
            skCircle(sketch, "E181", {"center": v(10.5, 21.87) * mm, "radius": 5.56 * mm});
            skCircle(sketch, "E182", {"center": v(10.5, 5.16) * mm, "radius": 5.56 * mm});
            skCircle(sketch, "E183", {"center": v(27.26, 5.16) * mm, "radius": 5.56 * mm});
            skCircle(sketch, "E184", {"center": v(27.26, 21.87) * mm, "radius": 5.56 * mm});
            skCircle(sketch, "E185", {"center": v(40.76, 13.51) * mm, "radius": 3.97 * mm});
            skCircle(sketch, "E186", {"center": v(10.5, 55.3) * mm, "radius": 5.56 * mm});
            skCircle(sketch, "E187", {"center": v(27.26, 55.3) * mm, "radius": 5.56 * mm});
            skCircle(sketch, "E188", {"center": v(40.76, 46.94) * mm, "radius": 3.97 * mm});
            skCircle(sketch, "E189", {"center": v(10.5, 38.58) * mm, "radius": 5.56 * mm});
            skCircle(sketch, "E190", {"center": v(27.26, 38.58) * mm, "radius": 5.56 * mm});
            skCircle(sketch, "E191", {"center": v(40.76, 30.23) * mm, "radius": 3.97 * mm});
            skCircle(sketch, "E192", {"center": v(40.76, 63.65) * mm, "radius": 3.97 * mm});
            skCircle(sketch, "E193", {"center": v(40.76, 113.8) * mm, "radius": 3.97 * mm});
            skCircle(sketch, "E194", {"center": v(10.5, 105.44) * mm, "radius": 5.56 * mm});
            skCircle(sketch, "E195", {"center": v(27.26, 105.44) * mm, "radius": 5.56 * mm});
            skCircle(sketch, "E196", {"center": v(40.76, 97.08) * mm, "radius": 3.97 * mm});
            skCircle(sketch, "E197", {"center": v(40.76, 130.5) * mm, "radius": 3.97 * mm});
            skCircle(sketch, "E198", {"center": v(40.76, 80.37) * mm, "radius": 3.97 * mm});
            skCircle(sketch, "E199", {"center": v(27.26, 122.15) * mm, "radius": 5.56 * mm});
            skCircle(sketch, "E200", {"center": v(10.5, 122.15) * mm, "radius": 5.56 * mm});
            skCircle(sketch, "E201", {"center": v(27.26, 88.72) * mm, "radius": 5.56 * mm});
            skCircle(sketch, "E202", {"center": v(27.26, 72) * mm, "radius": 5.56 * mm});
            skCircle(sketch, "E203", {"center": v(10.5, 88.72) * mm, "radius": 5.56 * mm});
            skCircle(sketch, "E204", {"center": v(10.5, 72) * mm, "radius": 5.56 * mm});
            skCircle(sketch, "E205", {"center": v(27.26, 138.86) * mm, "radius": 5.56 * mm});
            skCircle(sketch, "E206", {"center": v(27.26, 172.29) * mm, "radius": 5.56 * mm});
            skCircle(sketch, "E207", {"center": v(27.26, 155.58) * mm, "radius": 5.56 * mm});
            skCircle(sketch, "E208", {"center": v(40.76, 147.22) * mm, "radius": 3.97 * mm});
            skCircle(sketch, "E209", {"center": v(10.5, 138.86) * mm, "radius": 5.56 * mm});
            skCircle(sketch, "E210", {"center": v(10.5, 155.58) * mm, "radius": 5.56 * mm});
            skCircle(sketch, "E211", {"center": v(10.5, 172.29) * mm, "radius": 5.56 * mm});
            skCircle(sketch, "E212", {"center": v(40.76, 163.93) * mm, "radius": 3.97 * mm});
            skCircle(sketch, "E213", {"center": v(43.84, 0) * mm, "radius": 1.47 * mm});
            skCircle(sketch, "E214", {"center": v(0, 177.44) * mm, "radius": 1.47 * mm});
            skCircle(sketch, "E215", {"center": v(33.5, 163.93) * mm, "radius": 1.02 * mm});
            skCircle(sketch, "E216", {"center": v(15, 147.22) * mm, "radius": 1.02 * mm});
            skCircle(sketch, "E217", {"center": v(33.5, 130.5) * mm, "radius": 1.02 * mm});
            skCircle(sketch, "E218", {"center": v(15, 113.8) * mm, "radius": 1.02 * mm});
            skCircle(sketch, "E219", {"center": v(33.5, 97.08) * mm, "radius": 1.02 * mm});
            skCircle(sketch, "E220", {"center": v(15, 80.37) * mm, "radius": 1.02 * mm});
            skCircle(sketch, "E221", {"center": v(33.5, 63.65) * mm, "radius": 1.02 * mm});
            skCircle(sketch, "E222", {"center": v(15, 46.94) * mm, "radius": 1.02 * mm});
            skCircle(sketch, "E223", {"center": v(33.5, 30.23) * mm, "radius": 1.02 * mm});
            skCircle(sketch, "E224", {"center": v(15, 13.51) * mm, "radius": 1.02 * mm});
            skCircle(sketch, "E225", {"center": v(0, 0) * mm, "radius": 1.47 * mm});
            skCircle(sketch, "E226", {"center": v(43.84, 177.44) * mm, "radius": 1.47 * mm});
            skSolve(sketch);
        }
        {
            var Q0;
            Q0 = qSketchRegion(id + "F4", true);
            extrude(context, id + "F5", {"entities" : qUnion([Q0]), "operationType" : NewBodyOperationType.REMOVE, "oppositeDirection" : true, "depth" : 25 * mm});
        }
    });
